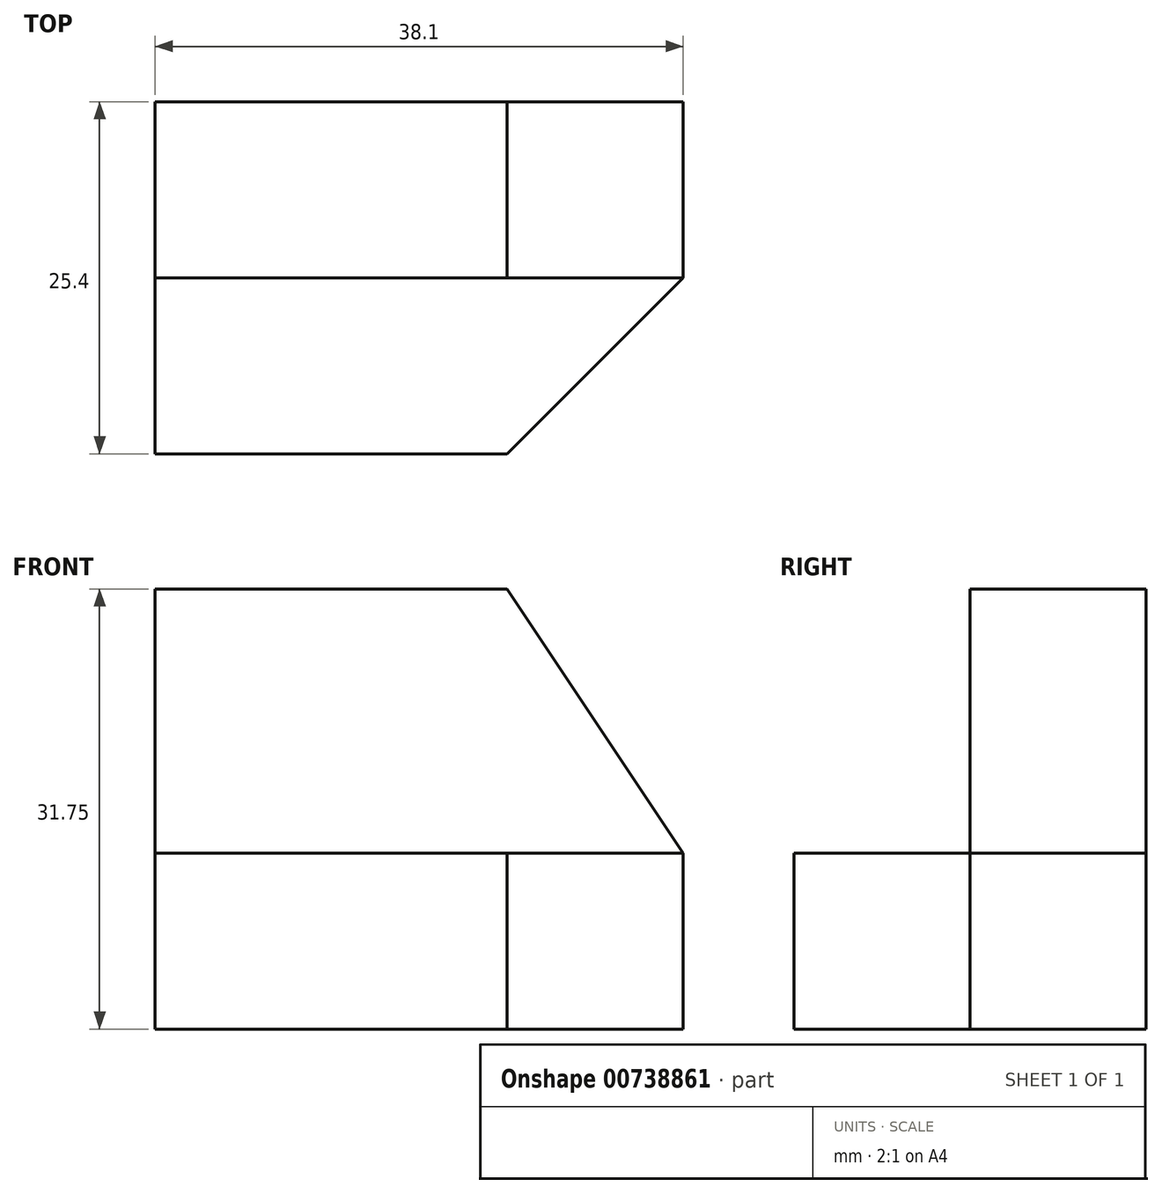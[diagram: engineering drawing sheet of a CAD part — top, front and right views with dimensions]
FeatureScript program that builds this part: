
annotation { "Feature Type Name" : "Feature", "Feature Type Description" : "" }
export const myFeature = defineFeature(function(context is Context, id is Id, definition is map)
    precondition{}
    {
        {
            var Q0;
            Q0=qCreatedBy(makeId("Front.planeOp"),FACE);
            var sketch = newSketch(context, id + "F0", { "sketchPlane" : qUnion([Q0])});
            skLineSegment(sketch, "E0", {"start": v(0, 31.75) * mm, "end": v(0, 0) * mm});
            skLineSegment(sketch, "E1", {"start": v(0, 0) * mm, "end": v(38.1, 0) * mm});
            skLineSegment(sketch, "E2", {"start": v(38.1, 0) * mm, "end": v(38.1, 31.75) * mm});
            skLineSegment(sketch, "E3", {"start": v(38.1, 31.75) * mm, "end": v(0, 31.75) * mm});
            skSolve(sketch);
        }
        {
            var Q0;
            Q0=makeQuery(id+"F0.imprint","IMPRINT",FACE,{"disambiguationData":[TD([[makeQuery(id+"F0.imprint","IMPRINT",EDGE,{"derivedFrom":sQuery(id+"F0.wireOp",EDGE,"E0")}),1.0]])]});
            extrude(context, id + "F1", {"entities" : qUnion([Q0]), "depth" : 25.4 * mm, "offsetDistance" : 25.4 * mm});
        }
        {
            var Q0;
            Q0=makeQuery(id+"F1.opExtrude","SWEPT_FACE",FACE,{"disambiguationData":[OSD([sQuery(id+"F0.wireOp",EDGE,"E2")])]});
            var sketch = newSketch(context, id + "F2", { "sketchPlane" : qUnion([Q0])});
            skLineSegment(sketch, "E4", {"start": v(-12.7, 31.75) * mm, "end": v(-12.7, 12.7) * mm});
            skLineSegment(sketch, "E5", {"start": v(-12.7, 12.7) * mm, "end": v(-25.4, 12.7) * mm});
            skSolve(sketch);
        }
        {
            var Q0;
            Q0=makeQuery(id+"F1.opExtrude","CAP_FACE",FACE,{"disambiguationData":[OSD([sQuery(id+"F0.wireOp",EDGE,"E0"),sQuery(id+"F0.wireOp",EDGE,"E1"),sQuery(id+"F0.wireOp",EDGE,"E2"),sQuery(id+"F0.wireOp",EDGE,"E3")])],"isStart":false});
            var sketch = newSketch(context, id + "F3", { "sketchPlane" : qUnion([Q0])});
            skLineSegment(sketch, "E6.bottom", {"start": v(0, 31.75) * mm, "end": v(38.1, 31.75) * mm});
            skLineSegment(sketch, "E6.top", {"start": v(0, 12.7) * mm, "end": v(38.1, 12.7) * mm});
            skLineSegment(sketch, "E6.left", {"start": v(0, 31.75) * mm, "end": v(0, 12.7) * mm});
            skLineSegment(sketch, "E6.right", {"start": v(38.1, 31.75) * mm, "end": v(38.1, 12.7) * mm});
            skSolve(sketch);
        }
        {
            var Q0;
            Q0 = qSketchRegion(id + "FmmBgkg6Cfn2SxC_1", true);
            var Q1;
            {var subQ0=sQuery(id+"F2.wireOp",EDGE,"E4");Q1=makeQuery(id+"F2.imprint","IMPRINT",FACE,{"disambiguationData":[TD([[makeQuery(id+"F2.imprint","IMPRINT",EDGE,{"derivedFrom":subQ0}),-1.0]])]});}
            extrude(context, id + "F4", {"entities" : qUnion([Q0, Q1]), "operationType" : NewBodyOperationType.REMOVE, "oppositeDirection" : true, "depth" : 12.7 * mm, "offsetDistance" : 25.4 * mm});
        }
        {
            var Q0;
            Q0=makeQuery(id+"F3.imprint","IMPRINT",FACE,{"disambiguationData":[TD([[makeQuery(id+"F3.imprint","IMPRINT",EDGE,{"derivedFrom":sQuery(id+"F3.wireOp",EDGE,"E6.bottom")}),1.0]])]});
            extrude(context, id + "F5", {"entities" : qUnion([Q0]), "operationType" : NewBodyOperationType.REMOVE, "oppositeDirection" : true, "depth" : 12.7 * mm, "offsetDistance" : 25.4 * mm});
        }
        {
            var Q0;
            Q0=makeQuery(id+"F5.boolean.opBoolean","MERGE",FACE,{"derivedFrom":[makeQuery(id+"F4.boolean.opBoolean","COPY",FACE,{"derivedFrom":makeQuery(id+"F4.opExtrude","SWEPT_FACE",FACE,{"disambiguationData":[OSD([sQuery(id+"F2.wireOp",EDGE,"E4")])]})}),makeQuery(id+"F5.opExtrude","CAP_FACE",FACE,{"disambiguationData":[OSD([sQuery(id+"F3.wireOp",EDGE,"E6.bottom"),sQuery(id+"F3.wireOp",EDGE,"E6.top"),sQuery(id+"F3.wireOp",EDGE,"E6.left"),sQuery(id+"F3.wireOp",EDGE,"E6.right")])],"isStart":false})]});
            var sketch = newSketch(context, id + "F6", { "sketchPlane" : qUnion([Q0])});
            skLineSegment(sketch, "E7", {"start": v(38.1, 12.7) * mm, "end": v(25.4, 31.75) * mm});
            skSolve(sketch);
        }
        {
            var Q0;
            {var subQ0=sQuery(id+"F6.wireOp",EDGE,"E7");Q0=makeQuery(id+"F6.imprint","IMPRINT",FACE,{"disambiguationData":[TD([[makeQuery(id+"F6.imprint","IMPRINT",EDGE,{"derivedFrom":subQ0}),-1.0]])]});}
            extrude(context, id + "F7", {"entities" : qUnion([Q0]), "operationType" : NewBodyOperationType.REMOVE, "endBound" : BoundingType.THROUGH_ALL, "oppositeDirection" : true, "depth" : 25.4 * mm, "offsetDistance" : 25.4 * mm});
        }
        {
            var Q0;
            Q0=makeQuery(id+"F5.boolean.opBoolean","MERGE",FACE,{"derivedFrom":[makeQuery(id+"F4.boolean.opBoolean","COPY",FACE,{"derivedFrom":makeQuery(id+"F4.opExtrude","SWEPT_FACE",FACE,{"disambiguationData":[OSD([sQuery(id+"F2.wireOp",EDGE,"E5")])]})}),makeQuery(id+"F5.opExtrude","SWEPT_FACE",FACE,{"disambiguationData":[OSD([sQuery(id+"F3.wireOp",EDGE,"E6.top")])]})]});
            var sketch = newSketch(context, id + "F8", { "sketchPlane" : qUnion([Q0])});
            skLineSegment(sketch, "E8", {"start": v(38.1, -12.7) * mm, "end": v(25.4, -25.4) * mm});
            skSolve(sketch);
        }
        {
            var Q0;
            {var subQ0=sQuery(id+"F8.wireOp",EDGE,"E8");Q0=makeQuery(id+"F8.imprint","IMPRINT",FACE,{"disambiguationData":[TD([[makeQuery(id+"F8.imprint","IMPRINT",EDGE,{"derivedFrom":subQ0}),1.0]])]});}
            extrude(context, id + "F9", {"entities" : qUnion([Q0]), "operationType" : NewBodyOperationType.REMOVE, "endBound" : BoundingType.THROUGH_ALL, "oppositeDirection" : true, "depth" : 25.4 * mm, "offsetDistance" : 25.4 * mm});
        }
    });
